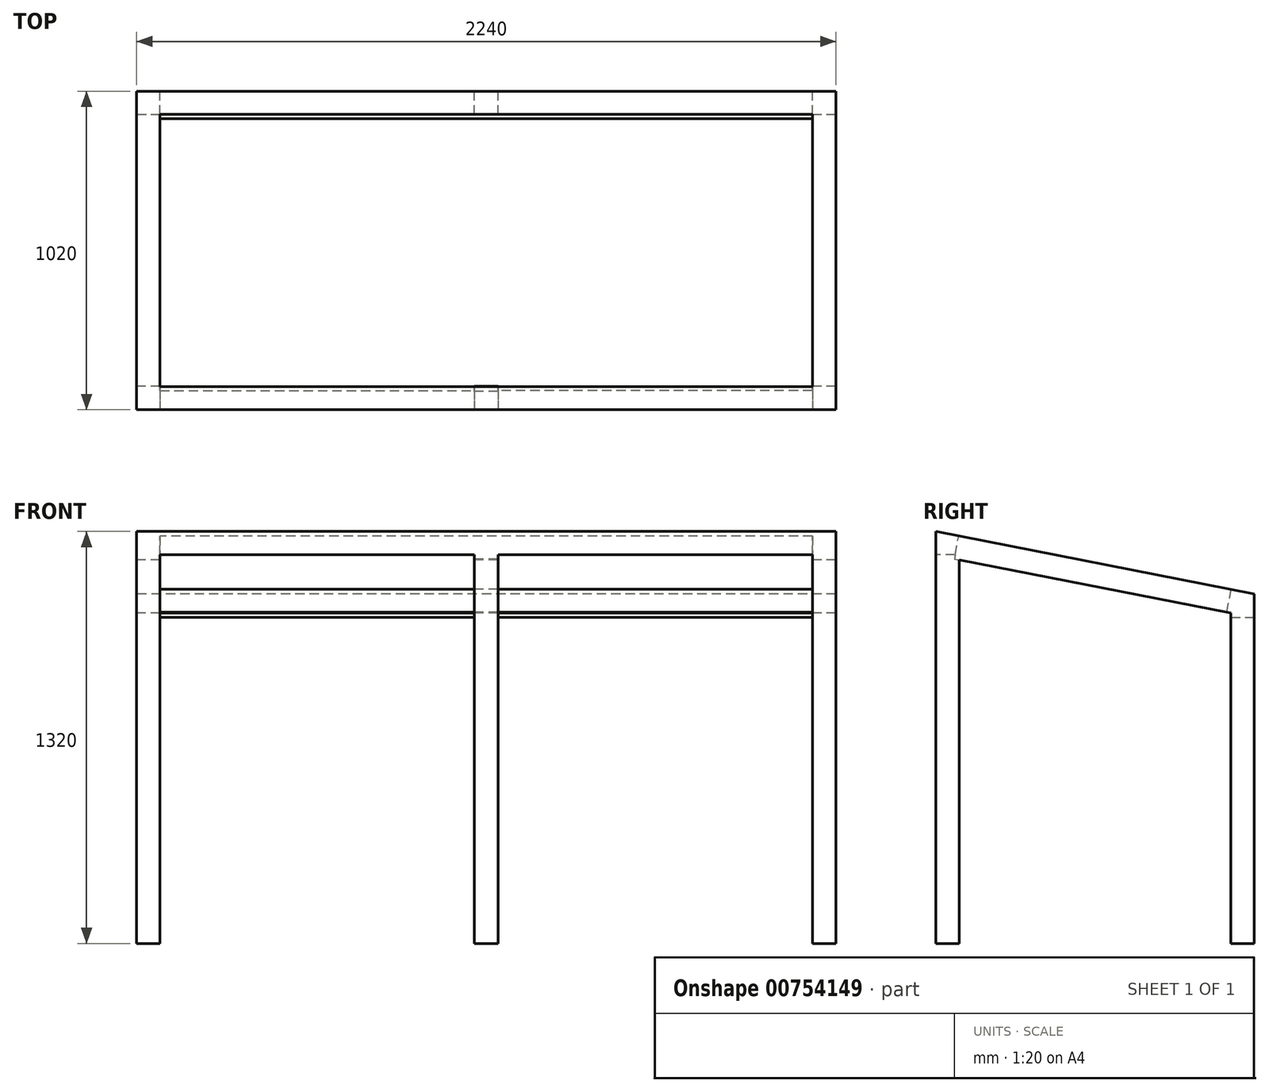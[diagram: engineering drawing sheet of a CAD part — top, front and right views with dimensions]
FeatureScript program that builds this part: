
annotation { "Feature Type Name" : "Feature", "Feature Type Description" : "" }
export const myFeature = defineFeature(function(context is Context, id is Id, definition is map)
    precondition{}
    {
        {
            var Q0;
            Q0=qCreatedBy(makeId("Front.planeOp"),FACE);
            var sketch = newSketch(context, id + "F0", { "sketchPlane" : qUnion([Q0])});
            skLineSegment(sketch, "E0.bottom", {"start": v(0, 0) * mm, "end": v(2240, 0) * mm});
            skLineSegment(sketch, "E0.top", {"start": v(0, 1320) * mm, "end": v(2240, 1320) * mm});
            skLineSegment(sketch, "E0.left", {"start": v(0, 0) * mm, "end": v(0, 1320) * mm});
            skLineSegment(sketch, "E0.right", {"start": v(2240, 0) * mm, "end": v(2240, 1320) * mm});
            skSolve(sketch);
        }
        {
            var Q0;
            Q0 = qSketchRegion(id + "F0", true);
            extrude(context, id + "F1", {"entities" : qUnion([Q0]), "oppositeDirection" : true, "depth" : 1020 * mm, "offsetDistance" : 25 * mm});
        }
        {
            var Q0;
            Q0=makeQuery(id+"F1.opExtrude","SWEPT_FACE",FACE,{"disambiguationData":[OSD([sQuery(id+"F0.wireOp",EDGE,"E0.left")])]});
            var sketch = newSketch(context, id + "F2", { "sketchPlane" : qUnion([Q0])});
            skLineSegment(sketch, "E1", {"start": v(0, 1320) * mm, "end": v(-1020, 1320) * mm});
            skLineSegment(sketch, "E2", {"start": v(-1020, 1320) * mm, "end": v(-1020, 1120) * mm});
            skLineSegment(sketch, "E3", {"start": v(-1020, 1120) * mm, "end": v(0, 1320) * mm});
            skSolve(sketch);
        }
        {
            var Q0;
            Q0 = qSketchRegion(id + "F2", true);
            extrude(context, id + "F3", {"entities" : qUnion([Q0]), "operationType" : NewBodyOperationType.REMOVE, "endBound" : BoundingType.THROUGH_ALL, "oppositeDirection" : true, "depth" : 25 * mm, "offsetDistance" : 25 * mm});
        }
        {
            var Q0;
            Q0=makeQuery(id+"F1.opExtrude","SWEPT_FACE",FACE,{"disambiguationData":[OSD([sQuery(id+"F0.wireOp",EDGE,"E0.left")])]});
            var sketch = newSketch(context, id + "F4", { "sketchPlane" : qUnion([Q0])});
            skLineSegment(sketch, "E4", {"start": v(-75, 0) * mm, "end": v(-75, 1228.87) * mm});
            skLineSegment(sketch, "E5", {"start": v(-75, 1228.87) * mm, "end": v(-945, 1058.28) * mm});
            skLineSegment(sketch, "E6", {"start": v(-945, 1058.28) * mm, "end": v(-945, 0) * mm});
            skLineSegment(sketch, "E7", {"start": v(-945, 0) * mm, "end": v(-75, 0) * mm});
            skSolve(sketch);
        }
        {
            var Q0;
            Q0 = qSketchRegion(id + "F4", true);
            extrude(context, id + "F5", {"entities" : qUnion([Q0]), "operationType" : NewBodyOperationType.REMOVE, "endBound" : BoundingType.THROUGH_ALL, "oppositeDirection" : true, "depth" : 25 * mm, "offsetDistance" : 25 * mm});
        }
        {
            var Q0;
            Q0=makeQuery(id+"F1.opExtrude","CAP_FACE",FACE,{"disambiguationData":[OSD([sQuery(id+"F0.wireOp",EDGE,"E0.bottom"),sQuery(id+"F0.wireOp",EDGE,"E0.top"),sQuery(id+"F0.wireOp",EDGE,"E0.left"),sQuery(id+"F0.wireOp",EDGE,"E0.right")])],"isStart":false});
            var sketch = newSketch(context, id + "F6", { "sketchPlane" : qUnion([Q0])});
            skLineSegment(sketch, "E8.left", {"start": v(-2165, 0) * mm, "end": v(-2165, 1045) * mm});
            skLineSegment(sketch, "E8.right", {"start": v(-75, 0) * mm, "end": v(-75, 1045) * mm});
            skLineSegment(sketch, "E9", {"start": v(-2165, 1045) * mm, "end": v(-1157.5, 1045) * mm});
            skLineSegment(sketch, "E10", {"start": v(-1157.5, 1045) * mm, "end": v(-1157.5, 0) * mm});
            skLineSegment(sketch, "E11", {"start": v(-1157.5, 0) * mm, "end": v(-2165, 0) * mm});
            skLineSegment(sketch, "E12", {"start": v(-75, 1045) * mm, "end": v(-1082.5, 1045) * mm});
            skLineSegment(sketch, "E13", {"start": v(-1082.5, 1045) * mm, "end": v(-1082.5, 0) * mm});
            skLineSegment(sketch, "E14", {"start": v(-1082.5, 0) * mm, "end": v(-75, 0) * mm});
            skSolve(sketch);
        }
        {
            var Q0;
            Q0 = qSketchRegion(id + "F6", true);
            extrude(context, id + "F7", {"entities" : qUnion([Q0]), "operationType" : NewBodyOperationType.REMOVE, "endBound" : BoundingType.UP_TO_NEXT, "oppositeDirection" : true, "depth" : 25 * mm, "offsetDistance" : 25 * mm});
        }
        {
            var Q0;
            Q0=makeQuery(id+"F1.opExtrude","CAP_FACE",FACE,{"disambiguationData":[OSD([sQuery(id+"F0.wireOp",EDGE,"E0.bottom"),sQuery(id+"F0.wireOp",EDGE,"E0.top"),sQuery(id+"F0.wireOp",EDGE,"E0.left"),sQuery(id+"F0.wireOp",EDGE,"E0.right")])],"isStart":true});
            var sketch = newSketch(context, id + "F8", { "sketchPlane" : qUnion([Q0])});
            skLineSegment(sketch, "E15.left", {"start": v(75, 0) * mm, "end": v(75, 1245) * mm});
            skLineSegment(sketch, "E15.right", {"start": v(2165, 0) * mm, "end": v(2165, 1245) * mm});
            skLineSegment(sketch, "E16", {"start": v(75, 1245) * mm, "end": v(1082.5, 1245) * mm});
            skLineSegment(sketch, "E17", {"start": v(1082.5, 1245) * mm, "end": v(1082.5, 0) * mm});
            skLineSegment(sketch, "E18", {"start": v(1082.5, 0) * mm, "end": v(75, 0) * mm});
            skLineSegment(sketch, "E19", {"start": v(2165, 1245) * mm, "end": v(1157.5, 1245) * mm});
            skLineSegment(sketch, "E20", {"start": v(1157.5, 1245) * mm, "end": v(1157.5, 0) * mm});
            skLineSegment(sketch, "E21", {"start": v(1157.5, 0) * mm, "end": v(2165, 0) * mm});
            skSolve(sketch);
        }
        {
            var Q0;
            Q0 = qSketchRegion(id + "F8", true);
            extrude(context, id + "F9", {"entities" : qUnion([Q0]), "operationType" : NewBodyOperationType.REMOVE, "oppositeDirection" : true, "depth" : 75 * mm, "offsetDistance" : 25 * mm});
        }
        {
            var Q0;
            Q0=makeQuery(id+"F3.boolean.opBoolean","COPY",FACE,{"derivedFrom":makeQuery(id+"F3.opExtrude","SWEPT_FACE",FACE,{"disambiguationData":[OSD([sQuery(id+"F2.wireOp",EDGE,"E3")])]})});
            var sketch = newSketch(context, id + "F10", { "sketchPlane" : qUnion([Q0])});
            skLineSegment(sketch, "E22.bottom", {"start": v(2165, -178.99) * mm, "end": v(75, -178.99) * mm});
            skLineSegment(sketch, "E22.top", {"start": v(2165, 710.44) * mm, "end": v(75, 710.44) * mm});
            skLineSegment(sketch, "E22.left", {"start": v(2165, -178.99) * mm, "end": v(2165, 710.44) * mm});
            skLineSegment(sketch, "E22.right", {"start": v(75, -178.99) * mm, "end": v(75, 710.44) * mm});
            skSolve(sketch);
        }
        {
            var Q0;
            Q0 = qSketchRegion(id + "F10", true);
            extrude(context, id + "F11", {"entities" : qUnion([Q0]), "operationType" : NewBodyOperationType.REMOVE, "oppositeDirection" : true, "depth" : 75 * mm, "offsetDistance" : 25 * mm});
        }
    });
